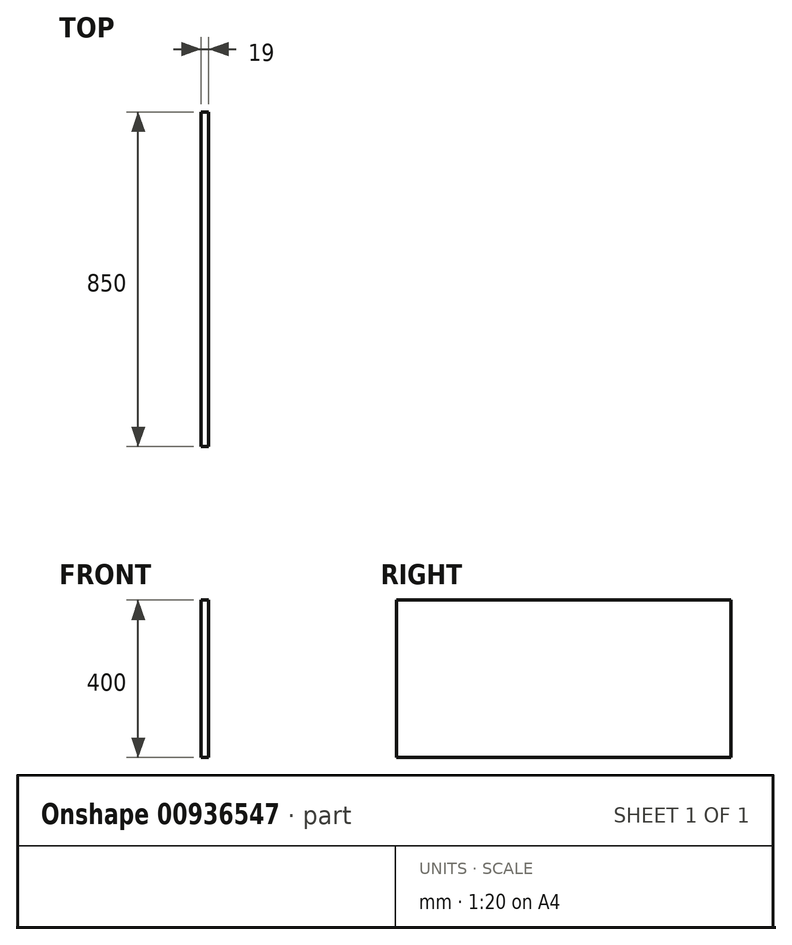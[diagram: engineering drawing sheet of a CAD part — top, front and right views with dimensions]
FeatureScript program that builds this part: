
annotation { "Feature Type Name" : "Feature", "Feature Type Description" : "" }
export const myFeature = defineFeature(function(context is Context, id is Id, definition is map)
    precondition{}
    {
        {
            var Q0;
            Q0=qCreatedBy(makeId("Front.planeOp"),FACE);
            var sketch = newSketch(context, id + "F0", { "sketchPlane" : qUnion([Q0])});
            skLineSegment(sketch, "E0.bottom", {"start": v(9.5, 200) * mm, "end": v(-9.5, 200) * mm});
            skLineSegment(sketch, "E0.top", {"start": v(9.5, -200) * mm, "end": v(-9.5, -200) * mm});
            skLineSegment(sketch, "E0.left", {"start": v(9.5, 200) * mm, "end": v(9.5, -200) * mm});
            skLineSegment(sketch, "E0.right", {"start": v(-9.5, 200) * mm, "end": v(-9.5, -200) * mm});
            skPoint(sketch, "E0.middle", {"position": v(0, 0) * mm});
            skSolve(sketch);
        }
        {
            var Q0;
            Q0=qSketchRegion(id+"F0",true);
            extrude(context, id + "F1", {"entities" : qUnion([Q0]), "depth" : 850 * mm, "offsetDistance" : 25 * mm});
        }
    });
